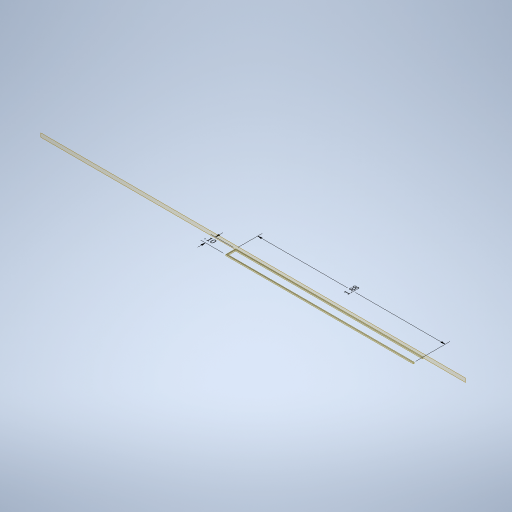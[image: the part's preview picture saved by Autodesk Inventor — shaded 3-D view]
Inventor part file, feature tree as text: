
AUTODESK INVENTOR PART (.ipt)
format: ipt  version: 2024.2 (Build 282272000, 272)  size: 275,968 bytes
history: native  units: in
note: dims shown in document units (in); Inventor stores cm internally (conversion verified against a paired STEP export)
features: other x3, plane x3, sketch x2, sweep x1
ambient origin geometry x8: Origin, YZ Plane, XZ Plane, XY Plane, X Axis, Y Axis, Z Axis, Center Point
bodies: Solid1 (feature_tree)
feature tree (9):
  other  "Annotations"
  sweep  "Sweep1"
  plane  "Work Plane1"
  plane  "Work Plane2"
  plane  "Work Plane4"
  sketch  "Sketch1"  dims[d6=0.0in d7=0.0in d11=0.25in d19=-0.25in]
  sketch  "Sketch2"  dims[d69=1.875in d70=1.875in d86=-0.1175in d89=0.1in d90=0.0in d91=0.0in d92=0.0in d98=0.01in d99=0.01in d100=0.1997in d101=1.875in d102=0.2692in d103=0.1197in d104=0.1in]
  other  "Linear Dimension 1"
  other  "Linear Dimension 2"
